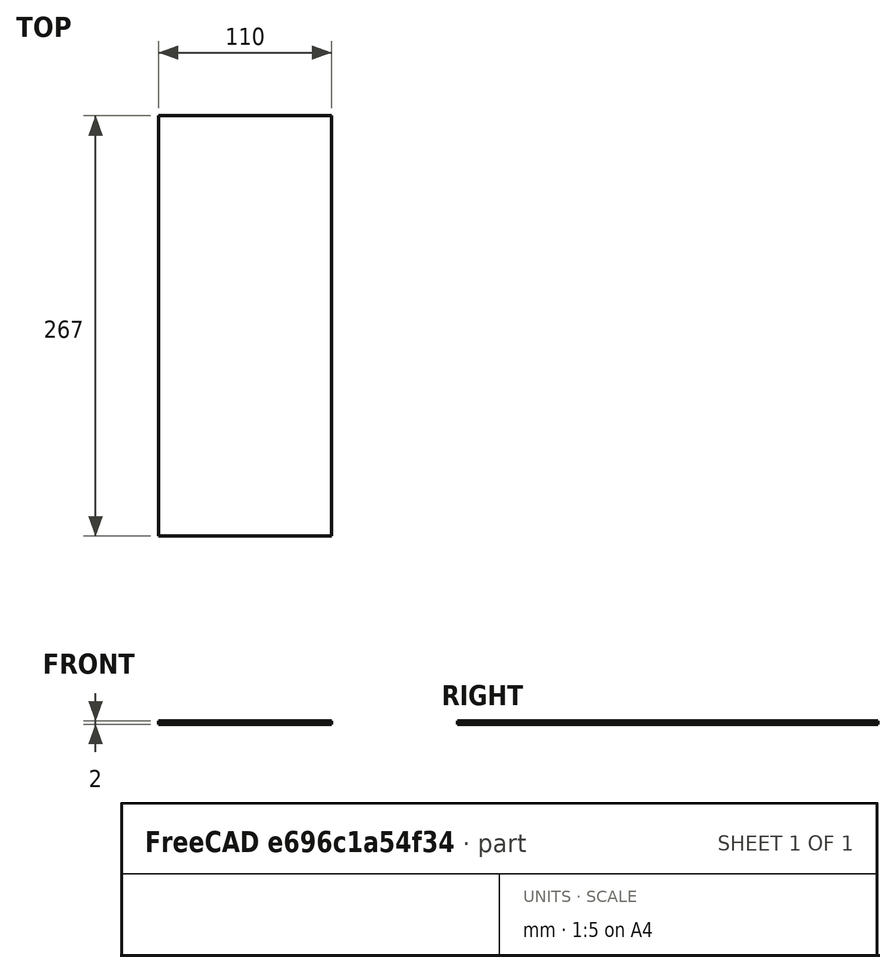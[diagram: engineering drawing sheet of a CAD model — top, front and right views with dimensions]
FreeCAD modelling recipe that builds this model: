
FCSTD DOCUMENT  (FreeCAD 1.0R39319 (Git))
Label: Acrylic_Backplate
License: All rights reserved
LicenseURL: https://en.wikipedia.org/wiki/All_rights_reserved
objects: Sketcher::SketchObject×1, PartDesign::Pad×1, PartDesign::Body×1, PartDesign::CoordinateSystem×1, App::Part×1
note: 7 computed .brp shape members not serialized (recipe doc carries the construction recipe); baked Part::Feature solids carry a one-line shape summary decoded from their .brp

FEATURE [Sketcher::SketchObject] Sketch
  ArcFitTolerance = 1e-06
  AttachmentSupport = -> [XY_Plane001]
  FullyConstrained = true
  MakeInternals = false
  MapMode = 5
  sketch-geometry (4):
    g0: LineSegment StartX=0 StartY=0 StartZ=0 EndX=110 EndY=0 EndZ=0
    g1: LineSegment StartX=110 StartY=0 StartZ=0 EndX=110 EndY=267 EndZ=0
    g2: LineSegment StartX=110 StartY=267 StartZ=0 EndX=0 EndY=267 EndZ=0
    g3: LineSegment StartX=0 StartY=267 StartZ=0 EndX=0 EndY=0 EndZ=0
  constraints (11):
    c: Coincident(g0,g1)
    c: Coincident(g1,g2)
    c: Coincident(g2,g3)
    c: Coincident(g3,g0)
    c: Horizontal(g0)
    c: Horizontal(g2)
    c: Vertical(g1)
    c: Vertical(g3)
    c: Coincident(g0,g-1)
    c: DistanceX(g2,g2) = 110
    c: DistanceY(g1,g1) = 267
FEATURE [PartDesign::Pad] Pad
  Direction = (0,0,1)
  Length = 2
  Length2 = 10
  Profile = -> Sketch
  ReferenceAxis = -> Sketch [N_Axis]
  Refine = true
  Suppressed = false
  Type = 0
FEATURE [PartDesign::Body] Body  label="Acrylic_Backplate001"
  AllowCompound = false
  Group = -> [Sketch,Pad]
  Origin = -> Origin001
  Tip = -> Pad
FEATURE [PartDesign::CoordinateSystem] LCS_1
  AttacherType = Attacher::AttachEngine3D
FEATURE [App::Part] Part  label="Acrylic_Backplate"
  Group = -> [Body,LCS_1]
  Origin = -> Origin
